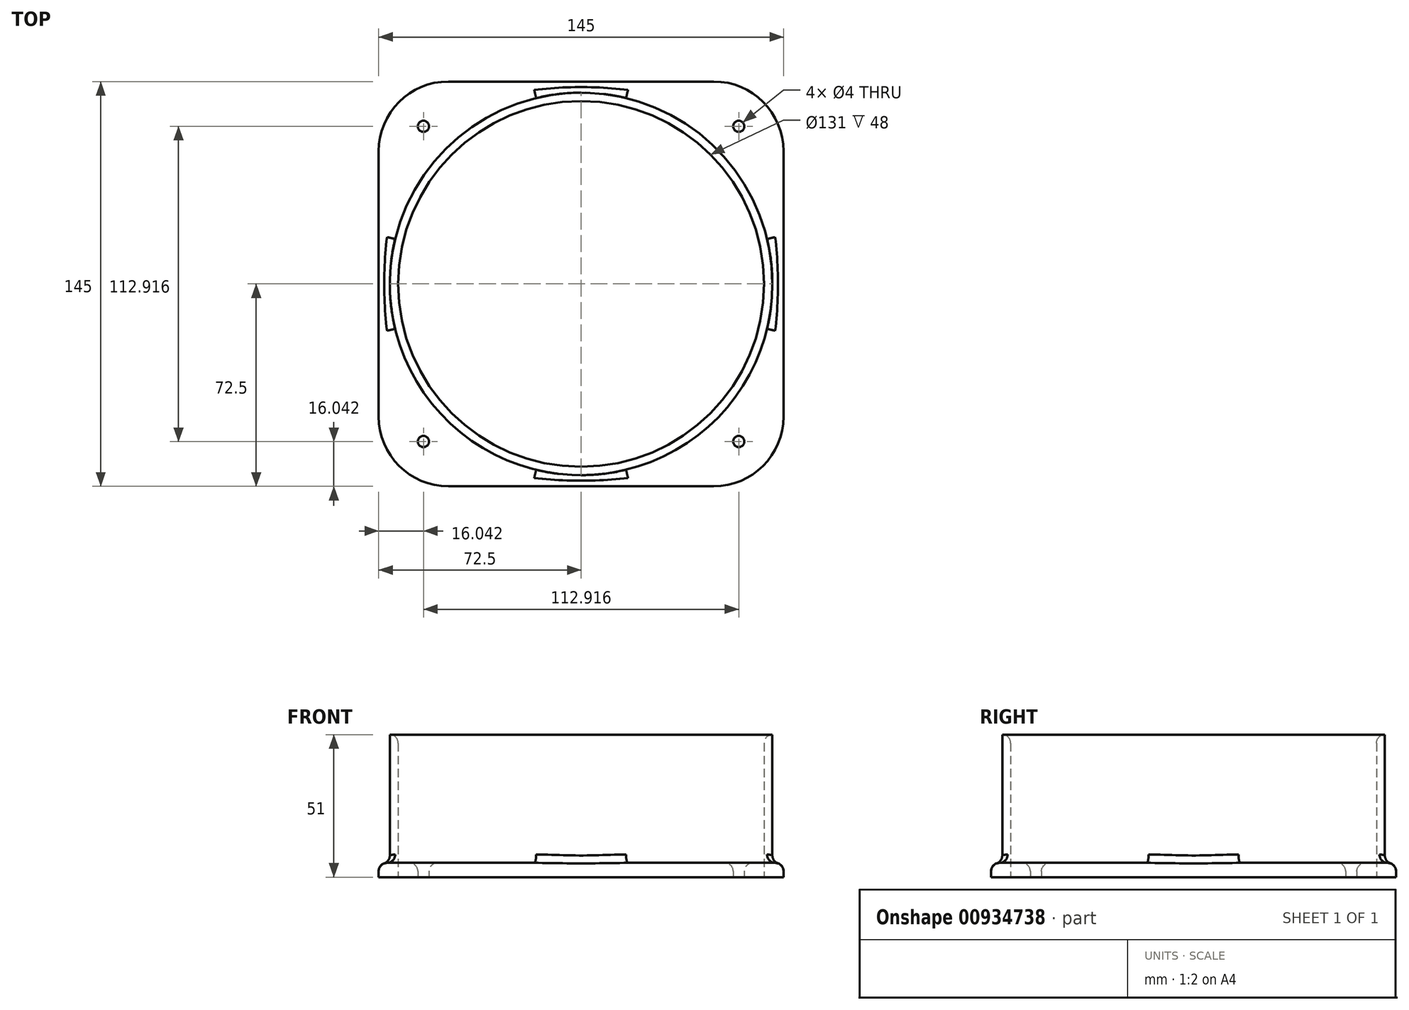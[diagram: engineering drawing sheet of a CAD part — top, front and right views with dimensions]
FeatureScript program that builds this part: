
annotation { "Feature Type Name" : "Feature", "Feature Type Description" : "" }
export const myFeature = defineFeature(function(context is Context, id is Id, definition is map)
    precondition{}
    {
        {
            var Q0;
            Q0=qCreatedBy(makeId("Top.planeOp"),FACE);
            var sketch = newSketch(context, id + "F0", { "sketchPlane" : qUnion([Q0])});
            skCircle(sketch, "E0", {"center": v(0, 0) * mm, "radius": 65.5 * mm});
            skCircle(sketch, "E1", {"center": v(0, 0) * mm, "radius": 68.5 * mm});
            skLineSegment(sketch, "E2.bottom", {"start": v(-72.5, 72.5) * mm, "end": v(72.5, 72.5) * mm});
            skLineSegment(sketch, "E2.top", {"start": v(-72.5, -72.5) * mm, "end": v(72.5, -72.5) * mm});
            skLineSegment(sketch, "E2.left", {"start": v(-72.5, 72.5) * mm, "end": v(-72.5, -72.5) * mm});
            skLineSegment(sketch, "E2.right", {"start": v(72.5, 72.5) * mm, "end": v(72.5, -72.5) * mm});
            skLineSegment(sketch, "E3", {"start": v(72.5, 72.5) * mm, "end": v(-72.5, -72.5) * mm, "construction": true});
            skCircle(sketch, "E4", {"center": v(-56.46, 56.46) * mm, "radius": 2 * mm});
            skCircle(sketch, "E5", {"center": v(56.46, -56.46) * mm, "radius": 2 * mm});
            skCircle(sketch, "E6", {"center": v(-56.46, -56.46) * mm, "radius": 2 * mm});
            skCircle(sketch, "E7", {"center": v(56.46, 56.46) * mm, "radius": 2 * mm});
            skLineSegment(sketch, "E8", {"start": v(-48.44, 48.44) * mm, "end": v(-56.46, 56.46) * mm, "construction": true});
            skLineSegment(sketch, "E9", {"start": v(-56.46, 56.46) * mm, "end": v(-64.48, 64.48) * mm, "construction": true});
            skLineSegment(sketch, "E10", {"start": v(-64.48, 64.48) * mm, "end": v(-72.5, 72.5) * mm, "construction": true});
            skLineSegment(sketch, "E11", {"start": v(48.44, -48.44) * mm, "end": v(56.46, -56.46) * mm, "construction": true});
            skSolve(sketch);
        }
        {
            var Q0;
            Q0=makeQuery(id+"F0.imprint","IMPRINT",FACE,{"disambiguationData":[TD([[makeQuery(id+"F0.imprint","IMPRINT",EDGE,{"derivedFrom":sQuery(id+"F0.wireOp",EDGE,"E0")}),-1.0]])]});
            extrude(context, id + "F1", {"entities" : qUnion([Q0]), "depth" : 51 * mm, "offsetDistance" : 25 * mm});
        }
        {
            var Q0;
            Q0=makeQuery(id+"F0.imprint","IMPRINT",FACE,{"disambiguationData":[TD([[makeQuery(id+"F0.imprint","IMPRINT",EDGE,{"derivedFrom":sQuery(id+"F0.wireOp",EDGE,"E1")}),-1.0]])]});
            extrude(context, id + "F2", {"entities" : qUnion([Q0]), "operationType" : NewBodyOperationType.ADD, "depth" : 5.1 * mm, "offsetDistance" : 25 * mm});
        }
        {
            var Q0;
            Q0=makeQuery(id+"F2.opExtrude","SWEPT_EDGE",EDGE,{"disambiguationData":[OSD([sQuery(id+"F0.wireOp",EDGE,"E2.top"),sQuery(id+"F0.wireOp",EDGE,"E2.right")])]});
            var Q1;
            Q1=makeQuery(id+"F2.opExtrude","SWEPT_EDGE",EDGE,{"disambiguationData":[OSD([sQuery(id+"F0.wireOp",EDGE,"E2.bottom"),sQuery(id+"F0.wireOp",EDGE,"E2.right")])]});
            var Q2;
            Q2=makeQuery(id+"F2.opExtrude","SWEPT_EDGE",EDGE,{"disambiguationData":[OSD([sQuery(id+"F0.wireOp",EDGE,"E2.bottom"),sQuery(id+"F0.wireOp",EDGE,"E2.left")])]});
            var Q3;
            Q3=makeQuery(id+"F2.opExtrude","SWEPT_EDGE",EDGE,{"disambiguationData":[OSD([sQuery(id+"F0.wireOp",EDGE,"E2.top"),sQuery(id+"F0.wireOp",EDGE,"E2.left")])]});
            fillet(context, id + "F3", {"entities" : qUnion([Q0, Q1, Q2, Q3]), "radius" : 25 * mm, "tangentPropagation" : true, "allowEdgeOverflow" : false});
        }
        {
            var Q0;
            Q0=makeQuery(id+"F2.opExtrude","CAP_EDGE",EDGE,{"disambiguationData":[OSD([sQuery(id+"F0.wireOp",EDGE,"E2.top")])],"isStart":false});
            fillet(context, id + "F4", {"entities" : qUnion([Q0]), "radius" : 3 * mm, "tangentPropagation" : true, "allowEdgeOverflow" : false});
        }
        {
            var Q0;
            Q0=makeQuery(id+"F2.opExtrude","CAP_EDGE",EDGE,{"disambiguationData":[OSD([sQuery(id+"F0.wireOp",EDGE,"E1")])],"isStart":false});
            var Q1;
            Q1=makeQuery(id+"F2.opExtrude","CAP_EDGE",EDGE,{"disambiguationData":[OSD([sQuery(id+"F0.wireOp",EDGE,"E5")])],"isStart":false});
            var Q2;
            Q2=makeQuery(id+"F2.opExtrude","CAP_EDGE",EDGE,{"disambiguationData":[OSD([sQuery(id+"F0.wireOp",EDGE,"E6")])],"isStart":false});
            var Q3;
            Q3=makeQuery(id+"F2.opExtrude","CAP_FACE",FACE,{"disambiguationData":[OSD([sQuery(id+"F0.wireOp",EDGE,"E1"),sQuery(id+"F0.wireOp",EDGE,"E2.bottom"),sQuery(id+"F0.wireOp",EDGE,"E2.top"),sQuery(id+"F0.wireOp",EDGE,"E2.left"),sQuery(id+"F0.wireOp",EDGE,"E2.right"),sQuery(id+"F0.wireOp",EDGE,"E4"),sQuery(id+"F0.wireOp",EDGE,"E5"),sQuery(id+"F0.wireOp",EDGE,"E6"),sQuery(id+"F0.wireOp",EDGE,"E7")])],"isStart":false});
            var Q4;
            Q4=makeQuery(id+"F1.opExtrude","CAP_EDGE",EDGE,{"disambiguationData":[OSD([sQuery(id+"F0.wireOp",EDGE,"E0")])],"isStart":false});
            fillet(context, id + "F5", {"entities" : qUnion([Q0, Q1, Q2, Q3, Q4]), "radius" : 3 * mm, "tangentPropagation" : true, "allowEdgeOverflow" : false});
        }
    });
